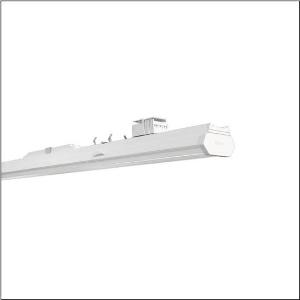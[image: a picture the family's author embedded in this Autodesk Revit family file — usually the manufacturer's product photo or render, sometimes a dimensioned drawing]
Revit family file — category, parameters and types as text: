
# Revit family: licross_r__11_protected_mo_51td1bdn49xg3s_1df8
name_source: partatom
category: Lighting Fixtures
units: mm (PartAtom-declared; Revit-internal decimal feet)

## family parameters
Cut with Voids When Loaded = No
Host = Face
Light Source = No
Part Type = Normal
Room Calculation Point = No
Round Connector Dimension = Use Diameter
Shared = No

## types (1)
- --- (1 x LED, 920 lm, 6.8 W, 4000K)
    Apparent Load = 7 VA
    CIE Flux Codes = 54 82 95 97 100
    Color Rendering = 80
    Color Temperature = 4000K
    Default Elevation = 1800 mm
    Description = Licross® 11 Protected MO, luminaire insert, of sheet steel, galvanised, coil coated, white, length: 1.500mm, width: 90mm, height: 101mm, LED rated luminous flux: 9.370lm, light colour: 840, control gear: DALI 2 (for two DALI lines), with plug, 6-pole, with phase selection, for trunking rail, 14-core, mains connection: 220..240V, AC, 50/60Hz, rated input power: 61W, for trunking rail, 14-core, halogen-free wiring, for emergency light function, converter,control gear: single battery element, battery: LiFePO4, 9Ah, primary optical cover: cover, of PMMA, light emission: direct distribution, primary light characteristic: symmetric, protection rating (complete): IP54, insulation class (complete): insulation class I (protective earthing), certification: CE, UKCA, protection symbol: D if used in an environment with non-conductive dust loads with corresponding accessories, impact resistance: IK06, permissible ambient temperature for indoor applications: +5..+35°C, standard: EN 60598-2-22, LABS conformity tested according to VDMA 24364:2018-05, reducing of maximum allowable ambient temperature of 5°C with ceiling mounting, corresponds to IFS (International Featured Standards) requirements for safety and quality in the food industry, packaging unit: 1 piece
    Height = 92 mm
    Lamp = 1 x LED
    Lamp Light Flux = 920 lm
    Lamp Power = 6.8 W
    Lamp count = 1
    Length = 1500 mm
    Luminous efficacy = 135 lm/W
    Manufacturer = Siteco
    ModVariant = No
    Model = 51TD1BDN49XG3S
    Mounting Place = Ceiling
    Mounting Type = Pendant
    Number of Poles = 1
    OnlyDefault = Yes
    Power Factor = 1
    Product Name = Licross® 11 Protected MO
    Product group = luminaire insert
    ProductGroupID = 901
    Protection Class = Protection class I
    Protection Degree = IP 54
    RLX_Detail_Level = 1
    RLX_Emergency_Light_Flux = 0 lm
    RLX_Emergency_Type = 0
    RLX_Emergency_Type_DB = No
    RlxData = <blob elided: 24709 chars, md5=19894c92>
    Socket = socket
    Standby Power = 0 W
    System Light Flux = 920 lm
    System Power = 7 W
    Type Comments = : emergency light operation: 3 h
    Type Image = l_1256145.jpg
    URL = http://relux.com
    VarID = @adj_059971
    Voltage = 0 V
    Weight = 0.00 kg
    Width = 88 mm

## geometry (parser evidence)
native form markers: Blend x4, Sweep x9
no freeform markers — native parametric forms only
